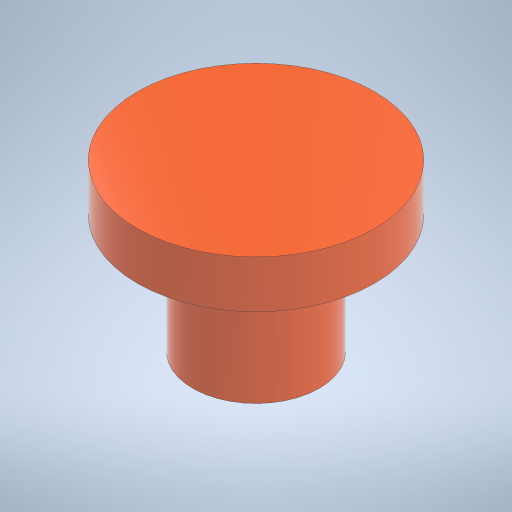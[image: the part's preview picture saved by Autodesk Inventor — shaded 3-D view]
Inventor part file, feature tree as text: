
AUTODESK INVENTOR PART (.ipt)
format: ipt  version: 2024 (Build 280153020, 153B)  size: 220,672 bytes
history: native  units: mm
features: extrude x2, sketch x2
ambient origin geometry x8: Origin, YZ Plane, XZ Plane, XY Plane, X Axis, Y Axis, Z Axis, Center Point
bodies: Solid1 (feature_tree)
feature tree (4):
  extrude  "Extrusion1"  Depth=3.0mm TaperAngle=0.0deg
  extrude  "Extrusion2"  Depth=7.5mm TaperAngle=0.0deg
  sketch  "Sketch1"  dims[d0=15.0mm d1=3.0mm d2=0.0mm]
  sketch  "Sketch2"  dims[d3=8.0mm d4=7.5mm d5=0.0mm]
